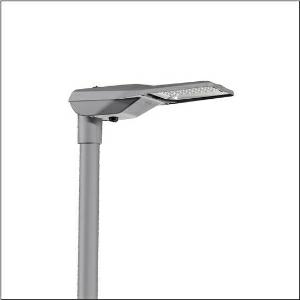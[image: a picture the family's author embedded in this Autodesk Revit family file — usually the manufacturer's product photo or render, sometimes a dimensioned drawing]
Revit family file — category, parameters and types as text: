
# Revit family: streetlight_sl_21_iq_mini___st1_0a_5xe2d31y08jb_55ca
name_source: partatom
category: Lighting Fixtures
units: mm (PartAtom-declared; Revit-internal decimal feet)

## family parameters
Cut with Voids When Loaded = No
Host = Face
Light Source = No
Part Type = Normal
Room Calculation Point = No
Round Connector Dimension = Use Diameter
Shared = No

## types (1)
- --- (1 x LED, 11210 lm, 72.5 W, 3000K)
    Apparent Load = 73 VA
    CIE Flux Codes = 40 73 97 100 100
    Color Rendering = 70
    Color Temperature = 3000K
    Default Elevation = 1800 mm
    Description = Streetlight SL 21 iQ mini, mast luminaire, primary light control with lens, of PMMA, primary optical cover: cover, of toughened safety glass, transparent, light distribution: ST1.0a, light emission: direct distribution, primary light characteristic: asymmetric, installation type: post-top, side-entry, LED, High Power LED, rated luminous flux: 11.210lm, luminous efficacy: 155lm/W, light colour: 730, colour temperature: 3000K, control gear: iQ-Street Remote, D4i with power reduction, control: pre-setting: logarithmic dimming characteristic, Street-Remote, Auto-Match, Temp-Guard, Lumen-Switch, Night-Set, Smart-Wire, Light-Fading, Desk-Remote (wireless, voltage-free reading and setting of iQ features in the workshop via application-optimized NFC function/RFID function), optimised constant luminous flux control (CLO 2.0), mains connection: 220..240V, AC, 50/60Hz, start of lifetime: 73W, end of service life: 76W, reduction: 33W, luminaire housing, of diecast aluminium, powder-coated, Siteco® metallic grey (DB 702S), corrosivity category C5 mid according to DIN EN ISO 12944, please order mast flange separately, inclination adjustable: 0°, 5°, 10°, 15°, sealing non-destructively replaceable, multi-level sealing system, length: 628mm, width: 235mm, height: 110mm, mast flange for spigot size: 42mm (side-entry): 5XC10008XM4, 60/48mm (side-entry/post-top): 5XC10108XM2, 76/60mm (side-entry/post-top): 5XC10108XM1, mounting height: 4..8m, Smart Interface below and above, protection rating (complete): IP66, insulation class (complete): insulation class II (safety insulation), certification: CE, ENEC, ENEC+, VDE, impact resistance: IK10, permissible operating ambient temperature for outdoor applications: -40..+50°C, standard-compliant lighting for roads and squares, packaging unit: 1 piece

Light Distribution: ST1.0a
    Height = 110 mm
    Lamp = 1 x LED
    Lamp Light Flux = 11210 lm
    Lamp Power = 72.5 W
    Lamp count = 1
    Length = 625 mm
    Luminous efficacy = 155 lm/W
    Manufacturer = Siteco
    ModVariant = No
    Model = 5XE2D31Y08JB
    Number of Poles = 1
    OnlyDefault = Yes
    Power Factor = 1
    Product Name = Streetlight SL 21 iQ mini | ST1.0a
    Product group = mast luminaire | pylon top
    ProductGroupID = 6100
    Protection Class = Protection class II
    Protection Degree = IP 66
    RLX_Detail_Level = 1
    RLX_Emergency_Light_Flux = 0 lm
    RLX_Emergency_Type = 0
    RLX_Emergency_Type_DB = No
    RlxData = <blob elided: 92405 chars, md5=fdf951ed>
    Socket = socket
    Standby Power = 0 W
    System Light Flux = 11210 lm
    System Power = 73 W
    Type Comments = factory setting: luminous flux: 100 % | dim-lin: 254 | 755 mA
    Type Image = l_1003514.jpg
    URL = http://relux.com
    VarID = @adj_135549
    Voltage = 0 V
    Weight = 0.00 kg
    Width = 234 mm

## geometry (parser evidence)
native form markers: Blend x4, Sweep x12
no freeform markers — native parametric forms only
